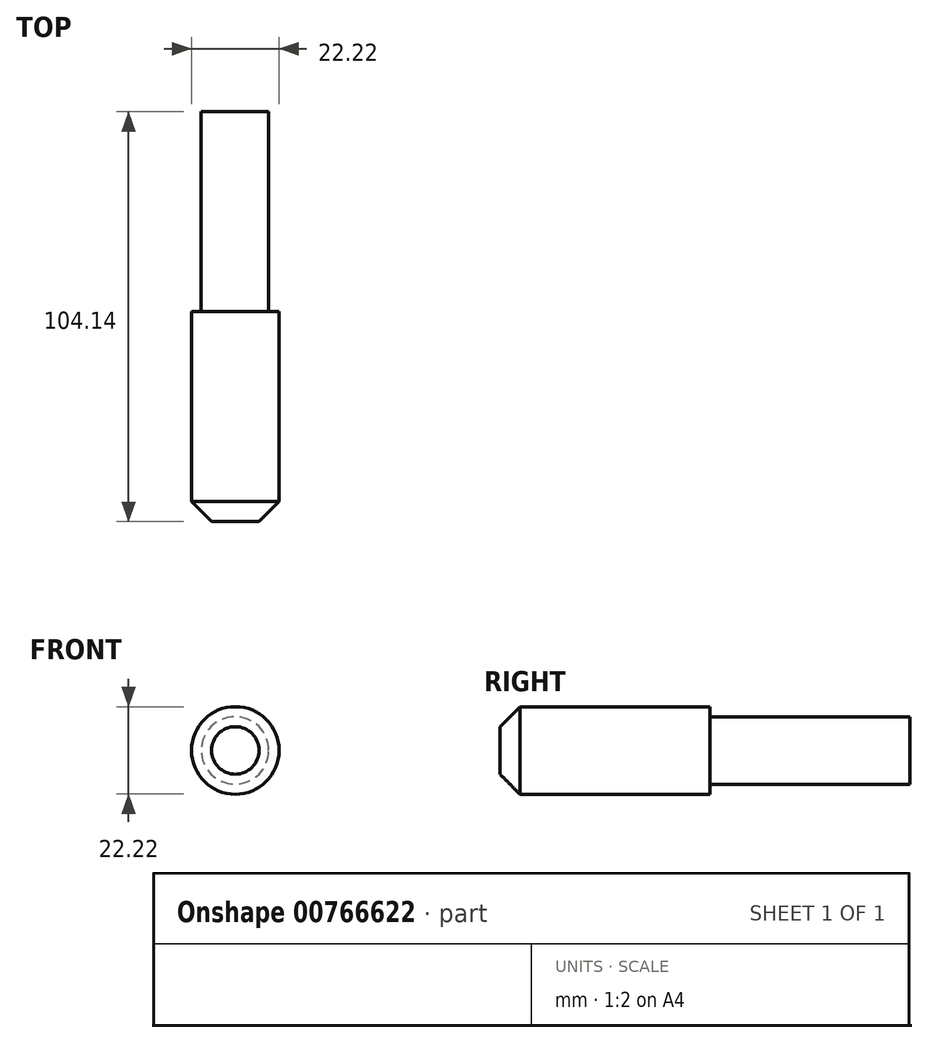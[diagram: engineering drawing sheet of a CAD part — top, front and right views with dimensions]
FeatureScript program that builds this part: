
annotation { "Feature Type Name" : "Feature", "Feature Type Description" : "" }
export const myFeature = defineFeature(function(context is Context, id is Id, definition is map)
    precondition{}
    {
        {
            var Q0;
            Q0=qCreatedBy(makeId("Front.planeOp"),FACE);
            var sketch = newSketch(context, id + "F0", { "sketchPlane" : qUnion([Q0])});
            skCircle(sketch, "E0", {"center": v(-37.68, 0) * mm, "radius": 11.11 * mm});
            skSolve(sketch);
        }
        {
            var Q0;
            Q0=makeQuery(id+"F0.imprint","IMPRINT",FACE,{"disambiguationData":[TD([[makeQuery(id+"F0.imprint","IMPRINT",EDGE,{"derivedFrom":sQuery(id+"F0.wireOp",EDGE,"E0")}),1.0]])]});
            var Q1;
            Q1=sQuery(id+"F0.wireOp",EDGE,"E0");
            extrude(context, id + "F1", {"entities" : qUnion([Q0]), "surfaceEntities" : qUnion([Q1]), "depth" : 53.34 * mm, "offsetDistance" : 25.4 * mm});
        }
        {
            var Q0;
            Q0=makeQuery(id+"F1.opExtrude","CAP_FACE",FACE,{"disambiguationData":[OSD([sQuery(id+"F0.wireOp",EDGE,"E0")])],"isStart":false});
            chamfer(context, id + "F2", {"entities" : qUnion([Q0]), "width" : 5.08 * mm, "tangentPropagation" : true});
        }
        {
            var Q0;
            Q0=makeQuery(id+"F0.imprint","IMPRINT",FACE,{"disambiguationData":[TD([[makeQuery(id+"F0.imprint","IMPRINT",EDGE,{"derivedFrom":sQuery(id+"F0.wireOp",EDGE,"E0")}),1.0]])]});
            var sketch = newSketch(context, id + "F3", { "sketchPlane" : qUnion([Q0])});
            skCircle(sketch, "E1", {"center": v(-37.77, 0) * mm, "radius": 8.57 * mm});
            skSolve(sketch);
        }
        {
            var Q0;
            Q0 = qSketchRegion(id + "F3", true);
            extrude(context, id + "F4", {"entities" : qUnion([Q0]), "operationType" : NewBodyOperationType.ADD, "oppositeDirection" : true, "depth" : 50.8 * mm, "offsetDistance" : 25.4 * mm});
        }
    });
